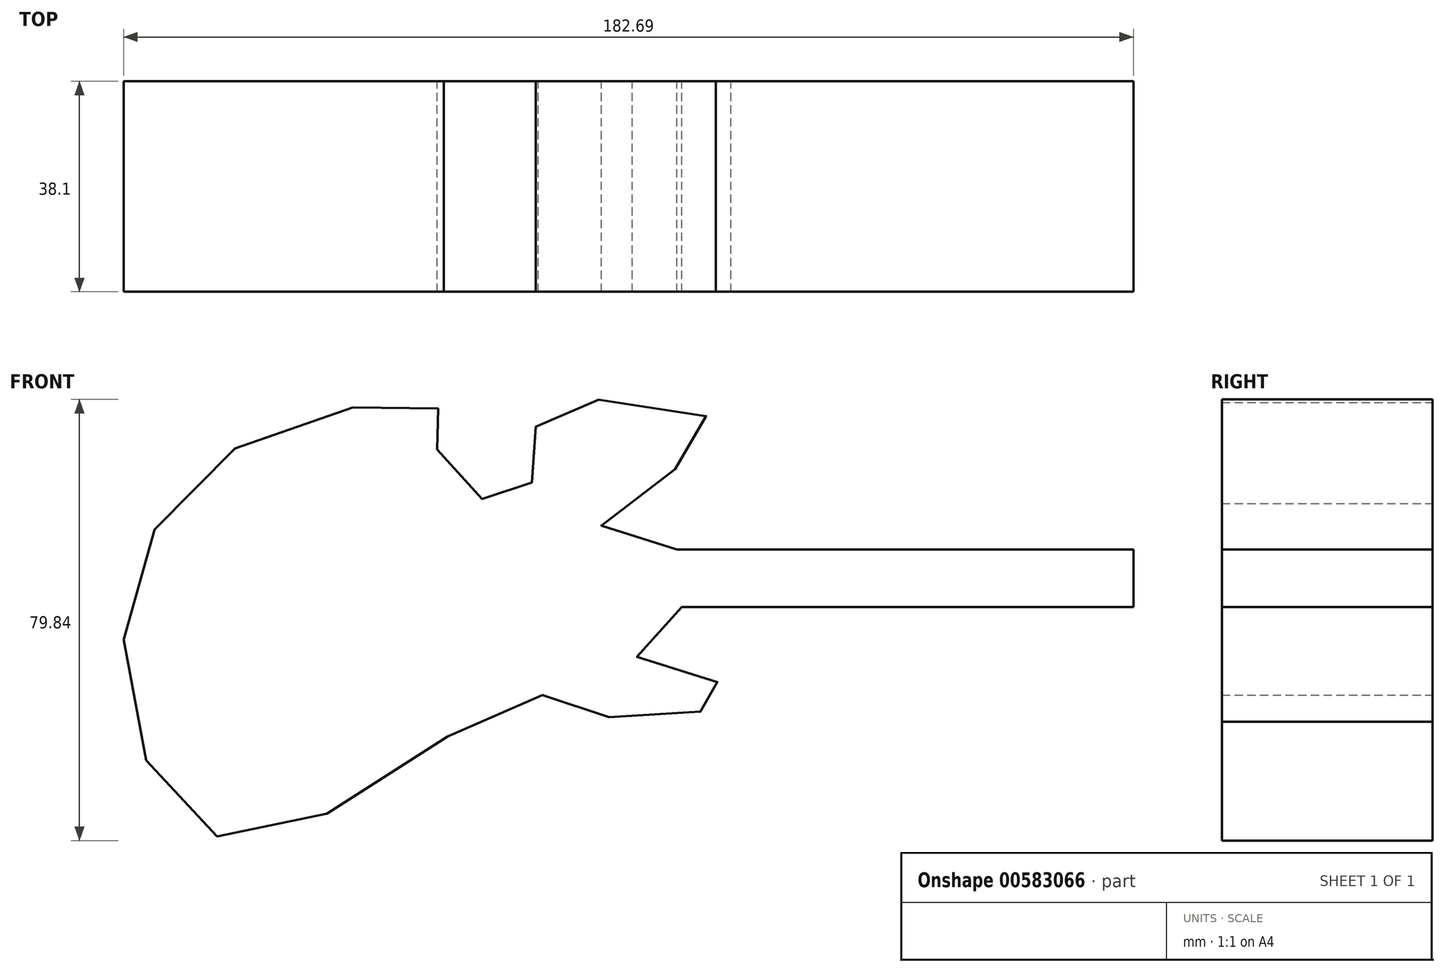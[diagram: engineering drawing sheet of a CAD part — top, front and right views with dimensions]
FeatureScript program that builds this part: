
annotation { "Feature Type Name" : "Feature", "Feature Type Description" : "" }
export const myFeature = defineFeature(function(context is Context, id is Id, definition is map)
    precondition{}
    {
        {
            var Q0;
            Q0=qCreatedBy(makeId("Front.planeOp"),FACE);
            var sketch = newSketch(context, id + "F0", { "sketchPlane" : qUnion([Q0])});
            skFitSpline(sketch, "E0", {"points": [v(-37.35, 38.19) * mm, v(-60.85, 0) * mm, v(-40.14, -34.55) * mm, v(11.89, -8.53) * mm, v(30.91, -13) * mm, v(48.82, -7.13) * mm, v(31.2, 0) * mm, v(48.54, 14.97) * mm, v(25.6, 21.96) * mm, v(46.3, 39.87) * mm, v(15.8, 43.5) * mm, v(14.13, 35.1) * mm, v(8.25, 26.44) * mm, v(-4.06, 35.67) * mm, v(-3.22, 42.94) * mm, v(-37.35, 38.19) * mm]});
            skLineSegment(sketch, "E1", {"start": v(39.27, 18.1) * mm, "end": v(121.84, 18.1) * mm});
            skLineSegment(sketch, "E2", {"start": v(121.84, 18.1) * mm, "end": v(121.84, 7.7) * mm});
            skLineSegment(sketch, "E3", {"start": v(121.84, 7.7) * mm, "end": v(48.82, 7.7) * mm});
            skLineSegment(sketch, "E4", {"start": v(48.82, 7.7) * mm, "end": v(40.14, 7.7) * mm});
            skSolve(sketch);
        }
        {
            var Q0;
            Q0 = qSketchRegion(id + "F0", true);
            extrude(context, id + "F1", {"entities" : qUnion([Q0]), "depth" : 38.1 * mm, "offsetDistance" : 25.4 * mm});
        }
    });
